# Revit family: P210876JX-026_JIC4324KB
name_source: partatom
category: Specialty Equipment
units: mm (PartAtom-declared; Revit-internal decimal feet)

## family parameters
Always vertical = Yes
Cut with Voids When Loaded = No
Enable Cutting in Views = No
Maintain Annotation Orientation = No
Part Type = Normal
Room Calculation Point = No
Round Connector Dimension = Use Diameter
Shared = No
Work Plane-Based = No

## types (1)
- JIC4324KB
    Amps = 0 A
    Body Material = ARCAT - Metal - Steel - Stainless
    Cooktop Glass Material = ARCAT - Glass - Tempered - Black Light
    Default Elevation = 0"
    Depth = 21 5/16"
    Description = Oblivion Glass 24" Induction Cooktop
Table de cuisson à surface en verre de 24 po
    Dimension Guide = https://www.whirlpool.com
https://www.whirlpool.com
    Family Name = Electric Built-In Cooktop
    Feature 1 = Assisted Cooking
Cuisson assistée
    Feature 2 = Emotive Controls
Commandes sensibles
    Feature 3 = Oblivion Glass Surface
Surface en verre hypnotisant
    Height = 3 29/32"
    Installation-Fabrication = https://whirlpool.com
https://whirlpool.com
    Manufacturer = JennAir
    Model = JIC4324KB
    Trim Material = ARCAT - Metal - Steel - Stainless
    Voltage = 0 V
    Width = 25 9/32"

## geometry (parser evidence)
native form markers: Sweep x4
no freeform markers — native parametric forms only
